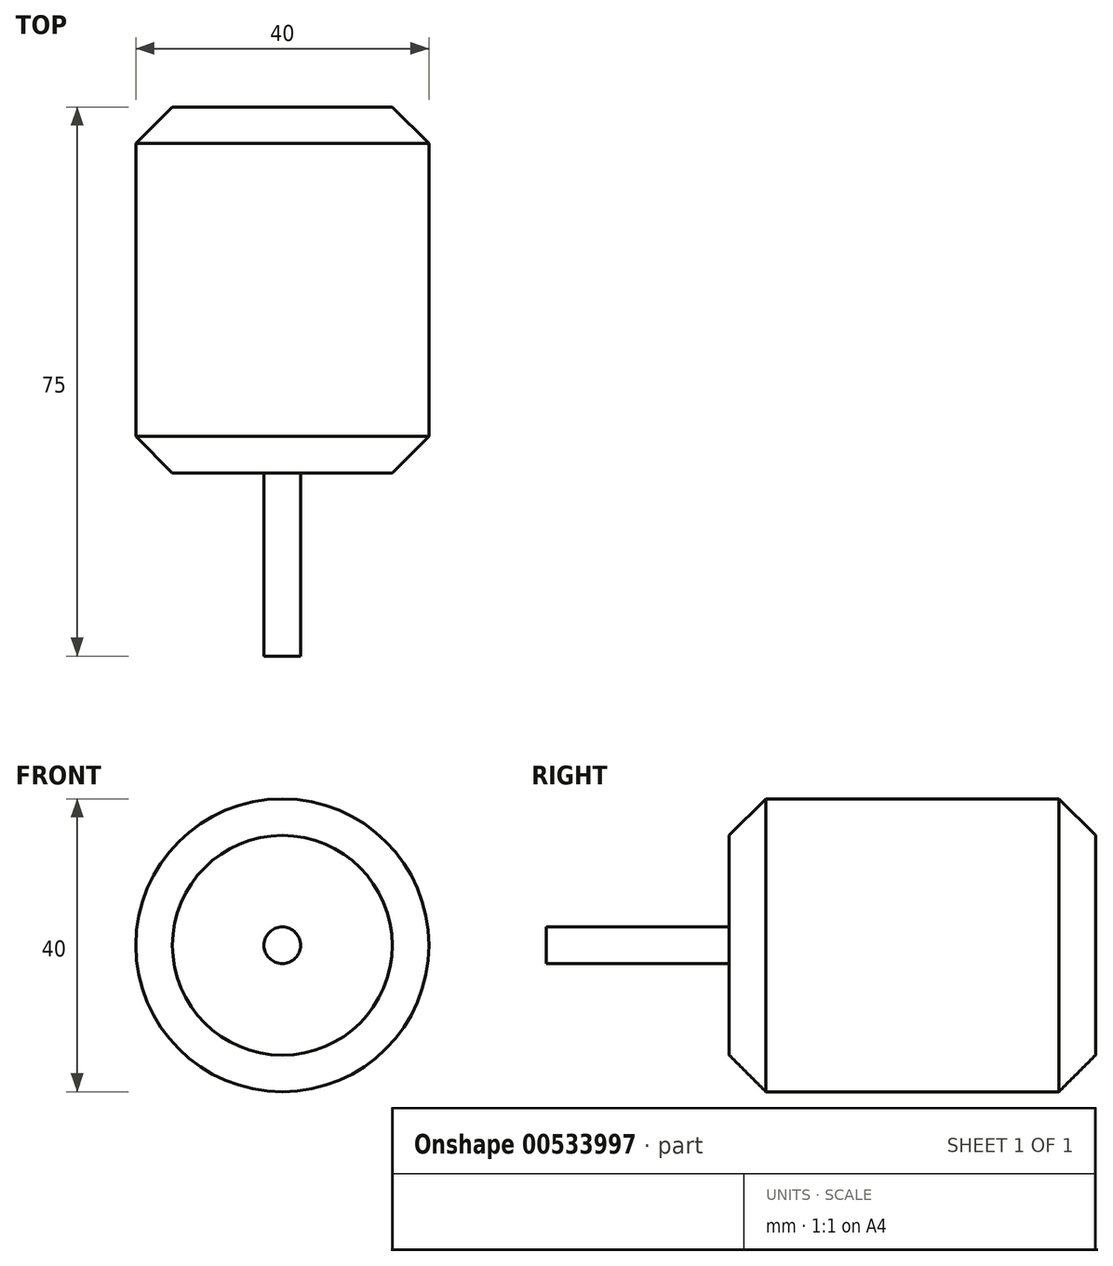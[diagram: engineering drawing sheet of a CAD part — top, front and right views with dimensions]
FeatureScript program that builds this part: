
annotation { "Feature Type Name" : "Feature", "Feature Type Description" : "" }
export const myFeature = defineFeature(function(context is Context, id is Id, definition is map)
    precondition{}
    {
        {
            var Q0;
            Q0=qCreatedBy(makeId("Front.planeOp"),FACE);
            var sketch = newSketch(context, id + "F0", { "sketchPlane" : qUnion([Q0])});
            skCircle(sketch, "E0", {"center": v(0, 0) * mm, "radius": 20 * mm});
            skSolve(sketch);
        }
        {
            var Q0;
            Q0 = qSketchRegion(id + "F0", true);
            extrude(context, id + "F1", {"entities" : qUnion([Q0]), "depth" : 50 * mm, "offsetDistance" : 25 * mm});
        }
        {
            var Q0;
            Q0=makeQuery(id+"F1.opExtrude","CAP_EDGE",EDGE,{"disambiguationData":[OSD([sQuery(id+"F0.wireOp",EDGE,"E0")])],"isStart":false});
            chamfer(context, id + "F2", {"entities" : qUnion([Q0]), "width" : 5 * mm, "tangentPropagation" : true});
        }
        {
            var Q0;
            Q0=makeQuery(id+"F1.opExtrude","CAP_FACE",FACE,{"disambiguationData":[OSD([sQuery(id+"F0.wireOp",EDGE,"E0")])],"isStart":false});
            var sketch = newSketch(context, id + "F3", { "sketchPlane" : qUnion([Q0])});
            skCircle(sketch, "E1", {"center": v(0, 0) * mm, "radius": 2.5 * mm});
            skSolve(sketch);
        }
        {
            var Q0;
            Q0=makeQuery(id+"F1.opExtrude","CAP_EDGE",EDGE,{"disambiguationData":[OSD([sQuery(id+"F0.wireOp",EDGE,"E0")])],"isStart":true});
            chamfer(context, id + "F4", {"entities" : qUnion([Q0]), "width" : 5 * mm, "tangentPropagation" : true});
        }
        {
            var Q0;
            Q0 = qSketchRegion(id + "F3", true);
            var Q1;
            Q1=sQuery(id+"F3.wireOp",EDGE,"E1");
            extrude(context, id + "F5", {"entities" : qUnion([Q0]), "surfaceEntities" : qUnion([Q1]), "depth" : 25 * mm, "offsetDistance" : 25 * mm});
        }
    });
